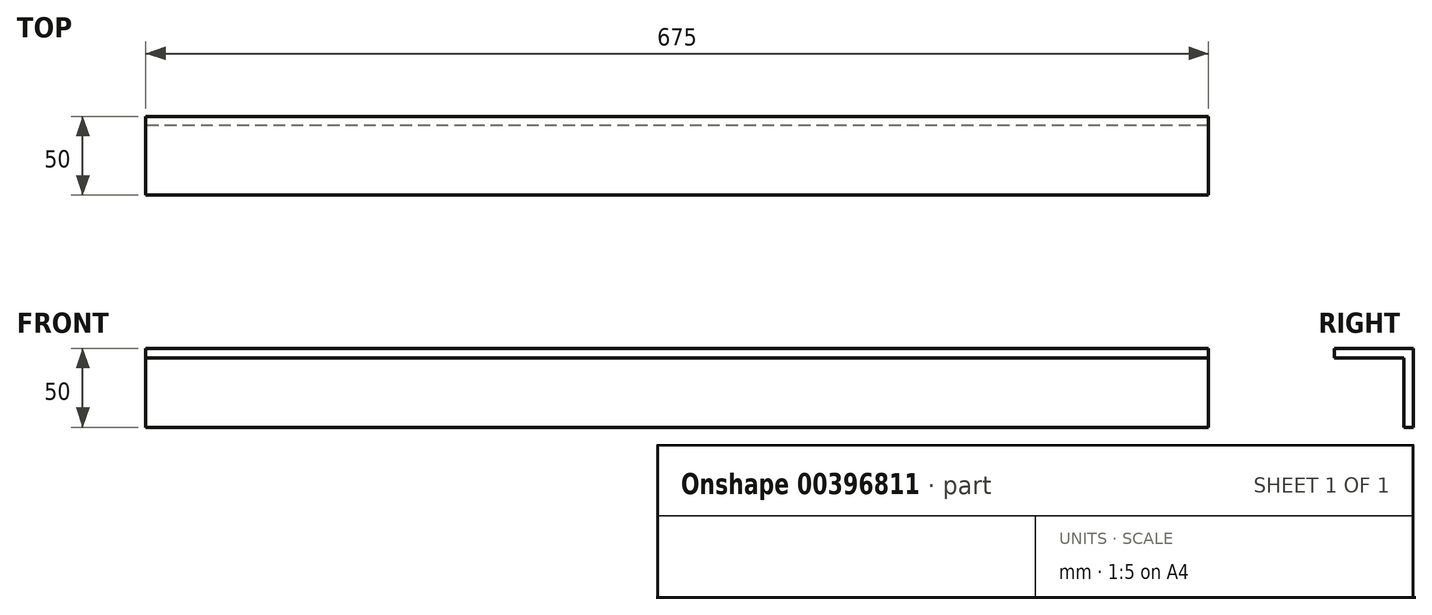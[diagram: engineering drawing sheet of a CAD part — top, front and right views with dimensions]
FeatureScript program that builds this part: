
annotation { "Feature Type Name" : "Feature", "Feature Type Description" : "" }
export const myFeature = defineFeature(function(context is Context, id is Id, definition is map)
    precondition{}
    {
        {
            var Q0;
            Q0=qCreatedBy(makeId("Right.planeOp"),FACE);
            var sketch = newSketch(context, id + "F0", { "sketchPlane" : qUnion([Q0])});
            skLineSegment(sketch, "E0", {"start": v(0, 0) * mm, "end": v(50, 0) * mm});
            skLineSegment(sketch, "E1", {"start": v(50, 0) * mm, "end": v(50, -50) * mm});
            skLineSegment(sketch, "E2", {"start": v(50, -50) * mm, "end": v(44, -50) * mm});
            skLineSegment(sketch, "E3", {"start": v(44, -50) * mm, "end": v(44, -6) * mm});
            skLineSegment(sketch, "E4", {"start": v(44, -6) * mm, "end": v(0, -6) * mm});
            skLineSegment(sketch, "E5", {"start": v(0, -6) * mm, "end": v(0, 0) * mm});
            skSolve(sketch);
        }
        {
            var Q0;
            Q0 = qSketchRegion(id + "F0", true);
            extrude(context, id + "F1", {"entities" : qUnion([Q0]), "endBound" : BoundingType.SYMMETRIC, "depth" : 675 * mm});
        }
    });
